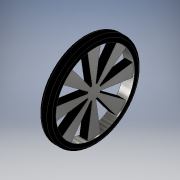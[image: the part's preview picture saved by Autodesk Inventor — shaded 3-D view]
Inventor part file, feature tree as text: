
AUTODESK INVENTOR PART (.ipt)
format: ipt  version: 2018 (Build 220112000, 112)  size: 211,456 bytes
history: native  units: in
note: dims shown in document units (in); Inventor stores cm internally (conversion verified against a paired STEP export)
features: extrude x3, sketch x3, fillet x1
ambient origin geometry x8: Origin, YZ Plane, XZ Plane, XY Plane, X Axis, Y Axis, Z Axis, Center Point
bodies: Solid1 (feature_tree)
feature tree (7):
  extrude  "Extrusion1"  Depth=2.3622in
  extrude  "Extrusion2"  Depth=0.3937in TaperAngle=360.0deg
  extrude  "Extrusion3"  Depth=0.0787in
  fillet  "Fillet1"  Radius=0.0394in
  sketch  "Sketch1"  dims[d0=2.7559in d1=2.3622in]
  sketch  "Sketch2"  dims[d2=0.3937in d3=3.1496in d5=360.0deg]
  sketch  "Sketch3"  dims[d7=0.315in d8=0.0in d9=2.3622in d10=0.0394in d11=0.0in d12=0.0394in d13=0.0in d14=0.0787in]
